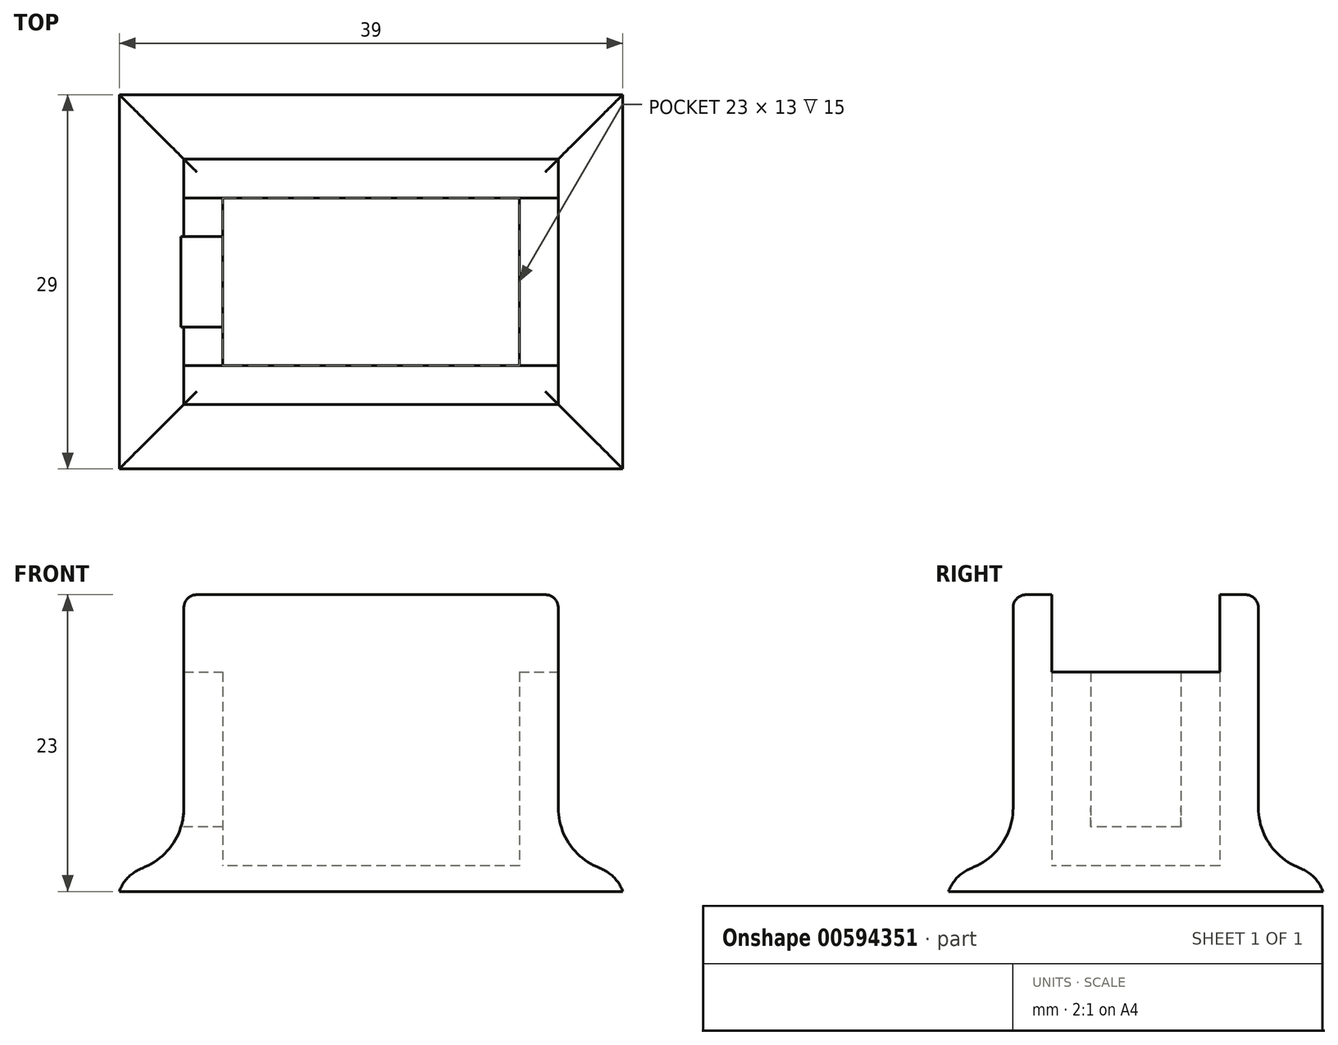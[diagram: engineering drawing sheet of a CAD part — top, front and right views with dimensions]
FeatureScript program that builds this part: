
annotation { "Feature Type Name" : "Feature", "Feature Type Description" : "" }
export const myFeature = defineFeature(function(context is Context, id is Id, definition is map)
    precondition{}
    {
        {
            var Q0;
            Q0=qCreatedBy(makeId("Top.planeOp"),FACE);
            var sketch = newSketch(context, id + "F0", { "sketchPlane" : qUnion([Q0])});
            skLineSegment(sketch, "E0.bottom", {"start": v(14.5, 9.5) * mm, "end": v(-14.5, 9.5) * mm});
            skLineSegment(sketch, "E0.top", {"start": v(14.5, -9.5) * mm, "end": v(-14.5, -9.5) * mm});
            skLineSegment(sketch, "E0.left", {"start": v(14.5, 9.5) * mm, "end": v(14.5, -9.5) * mm});
            skLineSegment(sketch, "E0.right", {"start": v(-14.5, 9.5) * mm, "end": v(-14.5, -9.5) * mm});
            skPoint(sketch, "E0.middle", {"position": v(0, 0) * mm});
            skLineSegment(sketch, "E1.bottom", {"start": v(11.5, 6.5) * mm, "end": v(-11.5, 6.5) * mm});
            skLineSegment(sketch, "E1.top", {"start": v(11.5, -6.5) * mm, "end": v(-11.5, -6.5) * mm});
            skLineSegment(sketch, "E1.left", {"start": v(11.5, 6.5) * mm, "end": v(11.5, -6.5) * mm});
            skLineSegment(sketch, "E1.right", {"start": v(-11.5, 6.5) * mm, "end": v(-11.5, -6.5) * mm});
            skLineSegment(sketch, "E2.bottom", {"start": v(19.5, 14.5) * mm, "end": v(-19.5, 14.5) * mm});
            skLineSegment(sketch, "E2.top", {"start": v(19.5, -14.5) * mm, "end": v(-19.5, -14.5) * mm});
            skLineSegment(sketch, "E2.left", {"start": v(19.5, 14.5) * mm, "end": v(19.5, -14.5) * mm});
            skLineSegment(sketch, "E2.right", {"start": v(-19.5, 14.5) * mm, "end": v(-19.5, -14.5) * mm});
            skLineSegment(sketch, "E3.bottom", {"start": v(-11.5, 3.5) * mm, "end": v(-14.5, 3.5) * mm});
            skLineSegment(sketch, "E3.top", {"start": v(-11.5, -3.5) * mm, "end": v(-14.5, -3.5) * mm});
            skLineSegment(sketch, "E3.left", {"start": v(-11.5, 3.5) * mm, "end": v(-11.5, -3.5) * mm});
            skLineSegment(sketch, "E3.right", {"start": v(-14.5, 3.5) * mm, "end": v(-14.5, -3.5) * mm});
            skSolve(sketch);
        }
        {
            var Q0;
            Q0=makeQuery(id+"F0.imprint","IMPRINT",FACE,{"disambiguationData":[TD([[makeQuery(id+"F0.imprint","IMPRINT",EDGE,{"derivedFrom":sQuery(id+"F0.wireOp",EDGE,"E0.bottom")}),1.0]])]});
            extrude(context, id + "F1", {"entities" : qUnion([Q0]), "depth" : 15 * mm, "offsetDistance" : 25 * mm});
        }
        {
            var Q0;
            Q0=makeQuery(id+"F0.imprint","IMPRINT",FACE,{"disambiguationData":[TD([[makeQuery(id+"F0.imprint","IMPRINT",EDGE,{"derivedFrom":sQuery(id+"F0.wireOp",EDGE,"E3.bottom")}),1.0]])]});
            extrude(context, id + "F2", {"entities" : qUnion([Q0]), "operationType" : NewBodyOperationType.ADD, "depth" : 3 * mm, "offsetDistance" : 25 * mm});
        }
        {
            var Q0;
            {var subQ1=sQuery(id+"F0.wireOp",EDGE,"E1.bottom");Q0=makeQuery(id+"F0.imprint","IMPRINT",FACE,{"disambiguationData":[TD([[makeQuery(id+"F0.imprint","IMPRINT",EDGE,{"derivedFrom":subQ1}),1.0]])]});}
            var Q1;
            {var subQ9=sQuery(id+"F0.wireOp",EDGE,"E0.bottom");Q1=makeQuery(id+"F0.imprint","IMPRINT",FACE,{"disambiguationData":[TD([[makeQuery(id+"F0.imprint","IMPRINT",EDGE,{"derivedFrom":subQ9}),1.0]])]});}
            var Q2;
            Q2=makeQuery(id+"F0.imprint","IMPRINT",FACE,{"disambiguationData":[TD([[makeQuery(id+"F0.imprint","IMPRINT",EDGE,{"derivedFrom":sQuery(id+"F0.wireOp",EDGE,"E3.bottom")}),1.0]])]});
            var Q3;
            {var subQ1=sQuery(id+"F0.wireOp",EDGE,"E0.bottom");Q3=makeQuery(id+"F0.imprint","IMPRINT",FACE,{"disambiguationData":[TD([[makeQuery(id+"F0.imprint","IMPRINT",EDGE,{"derivedFrom":subQ1}),-1.0]])]});}
            extrude(context, id + "F3", {"entities" : qUnion([Q0, Q1, Q2, Q3]), "operationType" : NewBodyOperationType.ADD, "oppositeDirection" : true, "depth" : 2 * mm, "offsetDistance" : 25 * mm});
        }
        {
            var Q0;
            Q0=makeQuery(id+"F3.opExtrude","CAP_EDGE",EDGE,{"disambiguationData":[OSD([sQuery(id+"F0.wireOp",EDGE,"E2.top")])],"isStart":true});
            var Q1;
            Q1=makeQuery(id+"F3.opExtrude","CAP_EDGE",EDGE,{"disambiguationData":[OSD([sQuery(id+"F0.wireOp",EDGE,"E2.right")])],"isStart":true});
            var Q2;
            Q2=makeQuery(id+"F3.opExtrude","CAP_EDGE",EDGE,{"disambiguationData":[OSD([sQuery(id+"F0.wireOp",EDGE,"E2.left")])],"isStart":true});
            var Q3;
            Q3=makeQuery(id+"F3.opExtrude","CAP_EDGE",EDGE,{"disambiguationData":[OSD([sQuery(id+"F0.wireOp",EDGE,"E2.bottom")])],"isStart":true});
            fillet(context, id + "F4", {"entities" : qUnion([Q0, Q1, Q2, Q3]), "radius" : 3 * mm, "tangentPropagation" : true, "allowEdgeOverflow" : false});
        }
        {
            var Q0;
            Q0=makeQuery(id+"F1.opExtrude","CAP_EDGE",EDGE,{"disambiguationData":[OSD([sQuery(id+"F0.wireOp",EDGE,"E0.top")])],"isStart":true});
            var Q1;
            {var subQ0=sQuery(id+"F0.wireOp",EDGE,"E3.right");var subQ1=sQuery(id+"F0.wireOp",EDGE,"E0.right");Q1=makeQuery(id+"F2.boolean.opBoolean","MERGE",EDGE,{"derivedFrom":[makeQuery(id+"F1.opExtrude","CAP_EDGE",EDGE,{"disambiguationData":[OSD([subQ1]),TDD([makeQuery(id+"F0.imprint","IMPRINT",EDGE,{"disambiguationData":[TD([[makeQuery(id+"F0.imprint","INTERSECT",VERTEX,{"derivedFrom":[sQuery(id+"F0.wireOp",EDGE,"E0.bottom"),subQ1]}),-1.0]])],"derivedFrom":subQ1})])],"isStart":true}),makeQuery(id+"F1.opExtrude","CAP_EDGE",EDGE,{"disambiguationData":[OSD([subQ1]),TDD([makeQuery(id+"F0.imprint","IMPRINT",EDGE,{"disambiguationData":[TD([[makeQuery(id+"F0.imprint","INTERSECT",VERTEX,{"derivedFrom":[sQuery(id+"F0.wireOp",EDGE,"E0.top"),subQ1]}),1.0]])],"derivedFrom":subQ1})])],"isStart":true}),makeQuery(id+"F2.opExtrude","CAP_EDGE",EDGE,{"disambiguationData":[OSD([subQ0])],"isStart":true})]});}
            var Q2;
            Q2=makeQuery(id+"F1.opExtrude","CAP_EDGE",EDGE,{"disambiguationData":[OSD([sQuery(id+"F0.wireOp",EDGE,"E0.left")])],"isStart":true});
            var Q3;
            Q3=makeQuery(id+"F1.opExtrude","CAP_EDGE",EDGE,{"disambiguationData":[OSD([sQuery(id+"F0.wireOp",EDGE,"E0.bottom")])],"isStart":true});
            fillet(context, id + "F5", {"entities" : qUnion([Q0, Q1, Q2, Q3]), "radius" : 5 * mm, "tangentPropagation" : true, "allowEdgeOverflow" : false});
        }
        {
            var Q0;
            Q0=makeQuery(id+"F1.opExtrude","CAP_FACE",FACE,{"disambiguationData":[OSD([sQuery(id+"F0.wireOp",EDGE,"E0.bottom"),sQuery(id+"F0.wireOp",EDGE,"E0.top"),sQuery(id+"F0.wireOp",EDGE,"E0.left"),sQuery(id+"F0.wireOp",EDGE,"E0.right"),sQuery(id+"F0.wireOp",EDGE,"E1.bottom"),sQuery(id+"F0.wireOp",EDGE,"E1.top"),sQuery(id+"F0.wireOp",EDGE,"E1.left"),sQuery(id+"F0.wireOp",EDGE,"E1.right"),sQuery(id+"F0.wireOp",EDGE,"E3.bottom"),sQuery(id+"F0.wireOp",EDGE,"E3.top")])],"isStart":false});
            var sketch = newSketch(context, id + "F6", { "sketchPlane" : qUnion([Q0])});
            skLineSegment(sketch, "E4", {"start": v(-11.5, 6.5) * mm, "end": v(-14.5, 6.5) * mm});
            skLineSegment(sketch, "E5", {"start": v(11.5, 6.5) * mm, "end": v(14.5, 6.5) * mm});
            skLineSegment(sketch, "E6", {"start": v(11.5, -6.5) * mm, "end": v(14.5, -6.5) * mm});
            skLineSegment(sketch, "E7", {"start": v(-11.5, -6.5) * mm, "end": v(-14.5, -6.5) * mm});
            skSolve(sketch);
        }
        {
            var Q0;
            Q0 = qSketchRegion(id + "F6", true);
            var Q1;
            {var subQ3=sQuery(id+"F6.wireOp",EDGE,"E4");Q1=makeQuery(id+"F6.imprint","IMPRINT",FACE,{"disambiguationData":[TD([[makeQuery(id+"F6.imprint","IMPRINT",EDGE,{"derivedFrom":subQ3}),-1.0]])]});}
            var Q2;
            {var subQ4=sQuery(id+"F6.wireOp",EDGE,"E6");Q2=makeQuery(id+"F6.imprint","IMPRINT",FACE,{"disambiguationData":[TD([[makeQuery(id+"F6.imprint","IMPRINT",EDGE,{"derivedFrom":subQ4}),-1.0]])]});}
            extrude(context, id + "F7", {"entities" : qUnion([Q0, Q1, Q2]), "operationType" : NewBodyOperationType.ADD, "depth" : 6 * mm, "offsetDistance" : 25 * mm});
        }
        {
            var Q0;
            Q0=makeQuery(id+"F7.opExtrude","CAP_EDGE",EDGE,{"disambiguationData":[OSD([sQuery(id+"F0.wireOp",EDGE,"E0.top")])],"isStart":false});
            var Q1;
            Q1=makeQuery(id+"F7.opExtrude","CAP_EDGE",EDGE,{"disambiguationData":[OSD([sQuery(id+"F0.wireOp",EDGE,"E0.bottom")])],"isStart":false});
            var Q2;
            {var subQ0=sQuery(id+"F0.wireOp",EDGE,"E0.left");var subQ1=makeQuery(id+"F1.opExtrude","CAP_EDGE",EDGE,{"disambiguationData":[OSD([subQ0])],"isStart":false});Q2=makeQuery(id+"F7.opExtrude","CAP_EDGE",EDGE,{"disambiguationData":[OSD([subQ0]),TDD([makeQuery(id+"F6.imprint","IMPRINT",EDGE,{"disambiguationData":[TD([[makeQuery(id+"F6.imprint","INTERSECT",VERTEX,{"derivedFrom":[makeQuery(id+"F1.opExtrude","CAP_EDGE",EDGE,{"disambiguationData":[OSD([sQuery(id+"F0.wireOp",EDGE,"E0.bottom")])],"isStart":false}),subQ1]}),-1.0]])],"derivedFrom":subQ1})])],"isStart":false});}
            var Q3;
            {var subQ0=sQuery(id+"F0.wireOp",EDGE,"E0.left");var subQ1=makeQuery(id+"F1.opExtrude","CAP_EDGE",EDGE,{"disambiguationData":[OSD([subQ0])],"isStart":false});Q3=makeQuery(id+"F7.opExtrude","CAP_EDGE",EDGE,{"disambiguationData":[OSD([subQ0]),TDD([makeQuery(id+"F6.imprint","IMPRINT",EDGE,{"disambiguationData":[TD([[makeQuery(id+"F6.imprint","INTERSECT",VERTEX,{"derivedFrom":[makeQuery(id+"F1.opExtrude","CAP_EDGE",EDGE,{"disambiguationData":[OSD([sQuery(id+"F0.wireOp",EDGE,"E0.top")])],"isStart":false}),subQ1]}),1.0]])],"derivedFrom":subQ1})])],"isStart":false});}
            var Q4;
            {var subQ0=sQuery(id+"F0.wireOp",EDGE,"E0.right");var subQ1=sQuery(id+"F0.wireOp",EDGE,"E0.bottom");var subQ2=makeQuery(id+"F1.opExtrude","CAP_EDGE",EDGE,{"disambiguationData":[OSD([subQ0]),TDD([makeQuery(id+"F0.imprint","IMPRINT",EDGE,{"disambiguationData":[TD([[makeQuery(id+"F0.imprint","INTERSECT",VERTEX,{"derivedFrom":[subQ1,subQ0]}),-1.0]])],"derivedFrom":subQ0})])],"isStart":false});Q4=makeQuery(id+"F7.opExtrude","CAP_EDGE",EDGE,{"disambiguationData":[OSD([subQ0]),TDD([makeQuery(id+"F6.imprint","IMPRINT",EDGE,{"disambiguationData":[TD([[makeQuery(id+"F6.imprint","INTERSECT",VERTEX,{"derivedFrom":[makeQuery(id+"F1.opExtrude","CAP_EDGE",EDGE,{"disambiguationData":[OSD([subQ1])],"isStart":false}),subQ2]}),-1.0]])],"derivedFrom":subQ2})])],"isStart":false});}
            var Q5;
            {var subQ0=sQuery(id+"F0.wireOp",EDGE,"E0.right");var subQ1=sQuery(id+"F0.wireOp",EDGE,"E0.top");var subQ2=makeQuery(id+"F1.opExtrude","CAP_EDGE",EDGE,{"disambiguationData":[OSD([subQ0]),TDD([makeQuery(id+"F0.imprint","IMPRINT",EDGE,{"disambiguationData":[TD([[makeQuery(id+"F0.imprint","INTERSECT",VERTEX,{"derivedFrom":[subQ1,subQ0]}),1.0]])],"derivedFrom":subQ0})])],"isStart":false});Q5=makeQuery(id+"F7.opExtrude","CAP_EDGE",EDGE,{"disambiguationData":[OSD([subQ0]),TDD([makeQuery(id+"F6.imprint","IMPRINT",EDGE,{"disambiguationData":[TD([[makeQuery(id+"F6.imprint","INTERSECT",VERTEX,{"derivedFrom":[makeQuery(id+"F1.opExtrude","CAP_EDGE",EDGE,{"disambiguationData":[OSD([subQ1])],"isStart":false}),subQ2]}),1.0]])],"derivedFrom":subQ2})])],"isStart":false});}
            fillet(context, id + "F8", {"entities" : qUnion([Q0, Q1, Q2, Q3, Q4, Q5]), "radius" : 1 * mm, "tangentPropagation" : true, "allowEdgeOverflow" : false});
        }
    });
